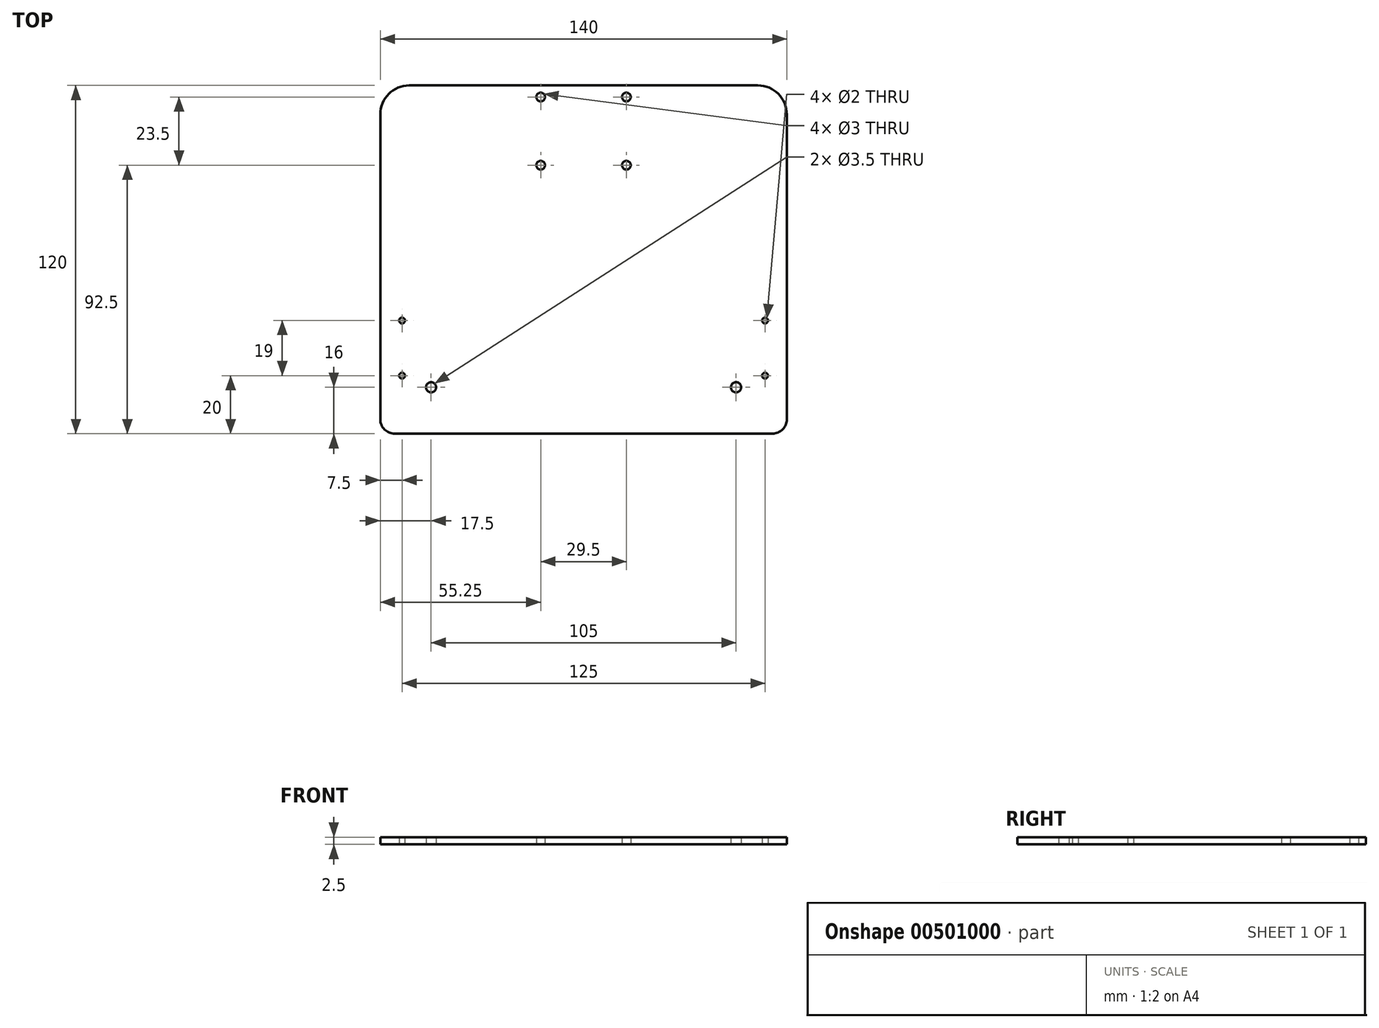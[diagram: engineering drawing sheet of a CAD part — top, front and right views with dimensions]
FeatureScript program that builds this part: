
annotation { "Feature Type Name" : "Feature", "Feature Type Description" : "" }
export const myFeature = defineFeature(function(context is Context, id is Id, definition is map)
    precondition{}
    {
        {
            var Q0;
            Q0=qCreatedBy(makeId("Top.planeOp"),FACE);
            var sketch = newSketch(context, id + "F0", { "sketchPlane" : qUnion([Q0])});
            skLineSegment(sketch, "E0.bottom", {"start": v(60, 60) * mm, "end": v(-60, 60) * mm});
            skLineSegment(sketch, "E0.top", {"start": v(65, -60) * mm, "end": v(-65, -60) * mm});
            skLineSegment(sketch, "E0.left", {"start": v(70, 50) * mm, "end": v(70, -55) * mm});
            skLineSegment(sketch, "E0.right", {"start": v(-70, 50) * mm, "end": v(-70, -55) * mm});
            skPoint(sketch, "E0.middle", {"position": v(0, 0) * mm});
            skCircle(sketch, "E1", {"center": v(-62.5, -40) * mm, "radius": 1 * mm});
            skCircle(sketch, "E2", {"center": v(-62.5, -21) * mm, "radius": 1 * mm});
            skCircle(sketch, "E3.MirrorC", {"center": v(62.5, -21) * mm, "radius": 1 * mm});
            skCircle(sketch, "E4.MirrorC", {"center": v(62.5, -40) * mm, "radius": 1 * mm});
            skCircle(sketch, "E5", {"center": v(14.75, 56) * mm, "radius": 1.5 * mm});
            skCircle(sketch, "E6", {"center": v(14.75, 32.5) * mm, "radius": 1.5 * mm});
            skCircle(sketch, "E7", {"center": v(-14.75, 56) * mm, "radius": 1.5 * mm});
            skCircle(sketch, "E8", {"center": v(-14.75, 32.5) * mm, "radius": 1.5 * mm});
            skPoint(sketch, "E9.visualSharp", {"position": v(-70, 60) * mm});
            skArc(sketch, "E9.filletArc", {"start": v(-60, 60) * mm, "mid": v(-67.07, 57.07) * mm, "end": v(-70, 50) * mm});
            skPoint(sketch, "E10.visualSharp", {"position": v(70, 60) * mm});
            skArc(sketch, "E10.filletArc", {"start": v(70, 50) * mm, "mid": v(67.07, 57.07) * mm, "end": v(60, 60) * mm});
            skPoint(sketch, "E11.visualSharp", {"position": v(-70, -60) * mm});
            skArc(sketch, "E11.filletArc", {"start": v(-70, -55) * mm, "mid": v(-68.54, -58.54) * mm, "end": v(-65, -60) * mm});
            skPoint(sketch, "E12.visualSharp", {"position": v(70, -60) * mm});
            skArc(sketch, "E12.filletArc", {"start": v(65, -60) * mm, "mid": v(68.54, -58.54) * mm, "end": v(70, -55) * mm});
            skCircle(sketch, "E13", {"center": v(-52.5, -44) * mm, "radius": 1.75 * mm});
            skCircle(sketch, "E14.MirrorC", {"center": v(52.5, -44) * mm, "radius": 1.75 * mm});
            skSolve(sketch);
        }
        {
            var Q0;
            Q0=makeQuery(id+"F0.imprint","IMPRINT",FACE,{"disambiguationData":[TD([[makeQuery(id+"F0.imprint","IMPRINT",EDGE,{"derivedFrom":sQuery(id+"F0.wireOp",EDGE,"E0.bottom")}),1.0]])]});
            extrude(context, id + "F1", {"entities" : qUnion([Q0]), "depth" : 2.5 * mm, "offsetDistance" : 25 * mm});
        }
    });
